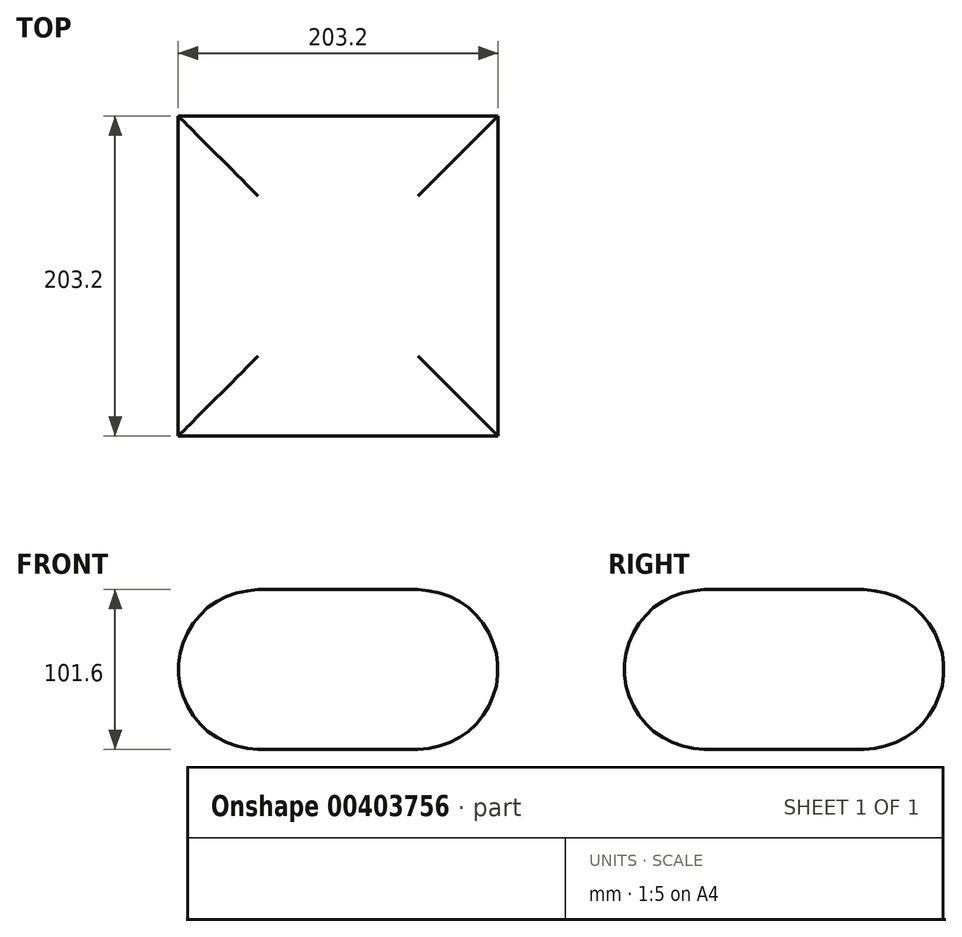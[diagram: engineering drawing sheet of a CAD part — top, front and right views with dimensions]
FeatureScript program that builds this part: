
annotation { "Feature Type Name" : "Feature", "Feature Type Description" : "" }
export const myFeature = defineFeature(function(context is Context, id is Id, definition is map)
    precondition{}
    {
        {
            var Q0;
            Q0=qCreatedBy(makeId("Top.planeOp"),FACE);
            var sketch = newSketch(context, id + "F0", { "sketchPlane" : qUnion([Q0])});
            skLineSegment(sketch, "E0.bottom", {"start": v(-101.6, 101.6) * mm, "end": v(101.6, 101.6) * mm});
            skLineSegment(sketch, "E0.top", {"start": v(-101.6, -101.6) * mm, "end": v(101.6, -101.6) * mm});
            skLineSegment(sketch, "E0.left", {"start": v(-101.6, 101.6) * mm, "end": v(-101.6, -101.6) * mm});
            skLineSegment(sketch, "E0.right", {"start": v(101.6, 101.6) * mm, "end": v(101.6, -101.6) * mm});
            skPoint(sketch, "E0.middle", {"position": v(0, 0) * mm});
            skSolve(sketch);
        }
        {
            var Q0;
            Q0 = qSketchRegion(id + "F0", true);
            extrude(context, id + "F1", {"entities" : qUnion([Q0]), "depth" : 101.6 * mm});
        }
        {
            var Q0;
            Q0=makeQuery(id+"F1.opExtrude","CAP_EDGE",EDGE,{"disambiguationData":[OSD([sQuery(id+"F0.wireOp",EDGE,"E0.left")])],"isStart":false});
            var Q1;
            Q1=makeQuery(id+"F1.opExtrude","CAP_EDGE",EDGE,{"disambiguationData":[OSD([sQuery(id+"F0.wireOp",EDGE,"E0.left")])],"isStart":true});
            var Q2;
            Q2=makeQuery(id+"F1.opExtrude","CAP_EDGE",EDGE,{"disambiguationData":[OSD([sQuery(id+"F0.wireOp",EDGE,"E0.right")])],"isStart":true});
            var Q3;
            Q3=makeQuery(id+"F1.opExtrude","CAP_EDGE",EDGE,{"disambiguationData":[OSD([sQuery(id+"F0.wireOp",EDGE,"E0.right")])],"isStart":false});
            var Q4;
            Q4=makeQuery(id+"F1.opExtrude","CAP_EDGE",EDGE,{"disambiguationData":[OSD([sQuery(id+"F0.wireOp",EDGE,"E0.top")])],"isStart":false});
            var Q5;
            Q5=makeQuery(id+"F1.opExtrude","CAP_EDGE",EDGE,{"disambiguationData":[OSD([sQuery(id+"F0.wireOp",EDGE,"E0.top")])],"isStart":true});
            var Q6;
            Q6=makeQuery(id+"F1.opExtrude","CAP_EDGE",EDGE,{"disambiguationData":[OSD([sQuery(id+"F0.wireOp",EDGE,"E0.bottom")])],"isStart":false});
            var Q7;
            Q7=makeQuery(id+"F1.opExtrude","CAP_EDGE",EDGE,{"disambiguationData":[OSD([sQuery(id+"F0.wireOp",EDGE,"E0.bottom")])],"isStart":true});
            fillet(context, id + "F2", {"entities" : qUnion([Q0, Q1, Q2, Q3, Q4, Q5, Q6, Q7]), "radius" : 50.8 * mm, "tangentPropagation" : true, "allowEdgeOverflow" : false});
        }
    });
